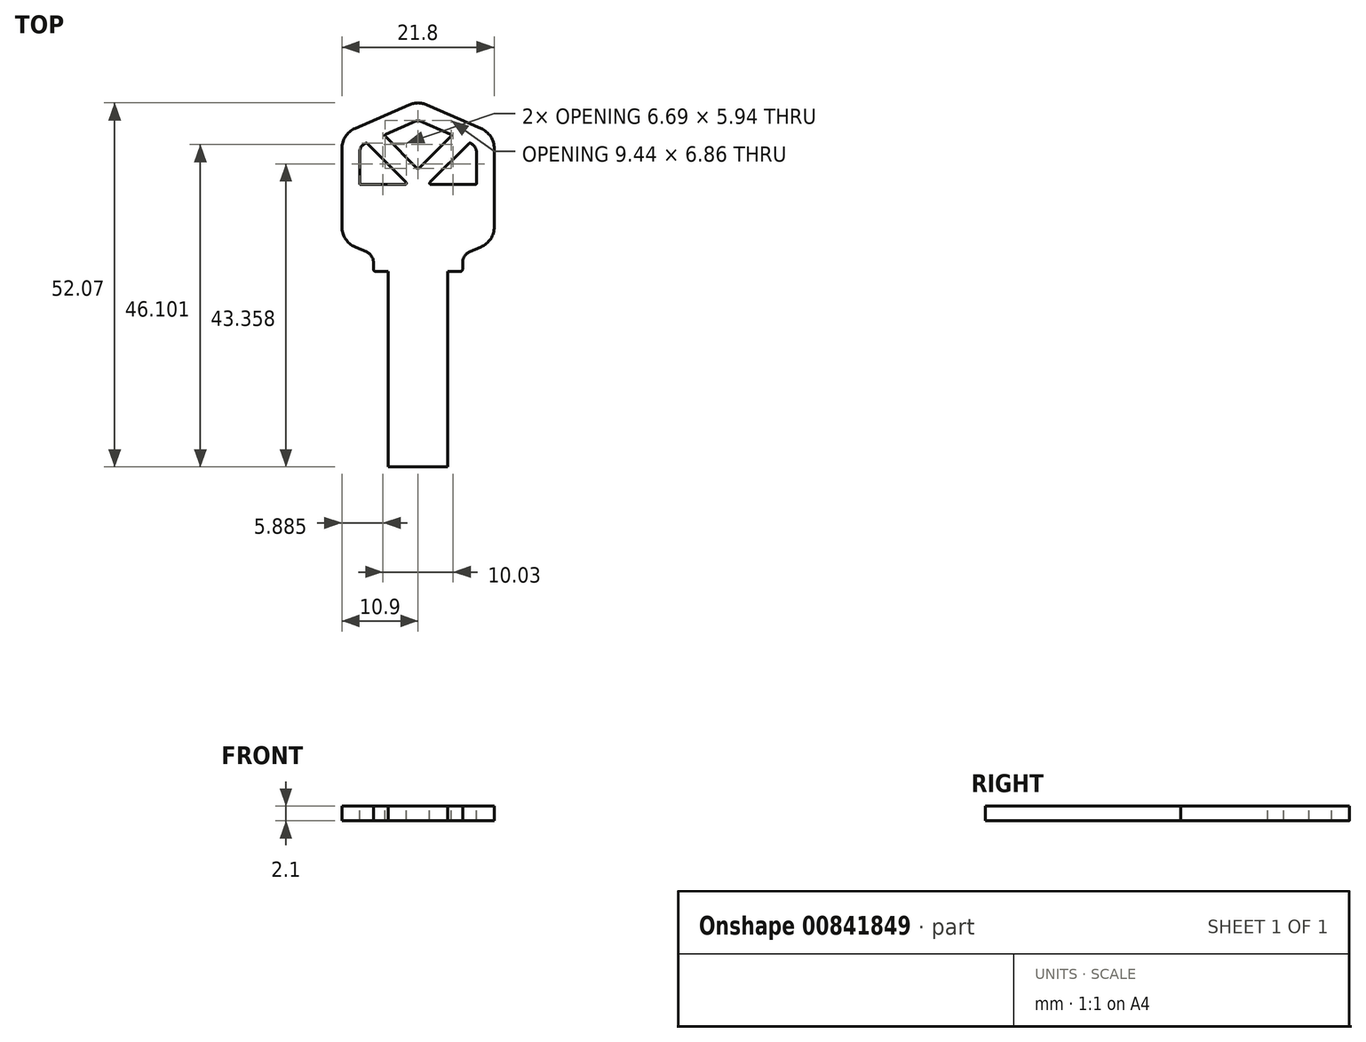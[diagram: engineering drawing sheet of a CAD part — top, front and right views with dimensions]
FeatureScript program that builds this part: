
annotation { "Feature Type Name" : "Feature", "Feature Type Description" : "" }
export const myFeature = defineFeature(function(context is Context, id is Id, definition is map)
    precondition{}
    {
        {
            var Q0;
            Q0=qCreatedBy(makeId("Top.planeOp"),FACE);
            var sketch = newSketch(context, id + "F0", { "sketchPlane" : qUnion([Q0])});
            skLineSegment(sketch, "E0", {"start": v(-1.27, -0.56) * mm, "end": v(-9, -3.93) * mm});
            skLineSegment(sketch, "E1", {"start": v(1.27, -0.56) * mm, "end": v(9, -3.93) * mm});
            skLineSegment(sketch, "E2", {"start": v(0, 0) * mm, "end": v(0, -52.36) * mm, "construction": true});
            skLineSegment(sketch, "E3", {"start": v(-10.9, -6.84) * mm, "end": v(-10.9, -17.99) * mm});
            skLineSegment(sketch, "E4", {"start": v(-9, -20.9) * mm, "end": v(-7.34, -21.62) * mm});
            skLineSegment(sketch, "E5", {"start": v(-6.39, -23.08) * mm, "end": v(-6.39, -24.42) * mm});
            skLineSegment(sketch, "E6", {"start": v(-6.39, -24.42) * mm, "end": v(-4.27, -24.42) * mm});
            skLineSegment(sketch, "E7", {"start": v(-4.27, -24.42) * mm, "end": v(-4.27, -52.36) * mm});
            skLineSegment(sketch, "E8", {"start": v(10.9, -6.84) * mm, "end": v(10.9, -17.99) * mm});
            skLineSegment(sketch, "E9", {"start": v(-10.9, -12.41) * mm, "end": v(0, -12.41) * mm, "construction": true});
            skLineSegment(sketch, "E10", {"start": v(0, -12.41) * mm, "end": v(10.9, -12.41) * mm, "construction": true});
            skLineSegment(sketch, "E11", {"start": v(9, -20.9) * mm, "end": v(7.34, -21.62) * mm});
            skLineSegment(sketch, "E12", {"start": v(6.39, -23.08) * mm, "end": v(6.39, -24.42) * mm});
            skLineSegment(sketch, "E13", {"start": v(6.39, -24.42) * mm, "end": v(4.27, -24.42) * mm});
            skLineSegment(sketch, "E14", {"start": v(4.27, -24.42) * mm, "end": v(4.27, -52.36) * mm});
            skLineSegment(sketch, "E15", {"start": v(-4.27, -52.36) * mm, "end": v(4.27, -52.36) * mm});
            skPoint(sketch, "E16.visualSharp", {"position": v(0, 0) * mm});
            skArc(sketch, "E16.filletArc", {"start": v(1.27, -0.56) * mm, "mid": v(0, -0.29) * mm, "end": v(-1.27, -0.56) * mm});
            skPoint(sketch, "E17.visualSharp", {"position": v(-10.9, -4.76) * mm});
            skArc(sketch, "E17.filletArc", {"start": v(-9, -3.93) * mm, "mid": v(-10.38, -5.1) * mm, "end": v(-10.9, -6.84) * mm});
            skPoint(sketch, "E18.visualSharp", {"position": v(10.9, -4.76) * mm});
            skArc(sketch, "E18.filletArc", {"start": v(10.9, -6.84) * mm, "mid": v(10.38, -5.1) * mm, "end": v(9, -3.93) * mm});
            skPoint(sketch, "E19", {"position": v(0, -0.29) * mm});
            skPoint(sketch, "E20.visualSharp", {"position": v(10.9, -20.07) * mm});
            skArc(sketch, "E20.filletArc", {"start": v(9, -20.9) * mm, "mid": v(10.38, -19.73) * mm, "end": v(10.9, -17.99) * mm});
            skPoint(sketch, "E21.visualSharp", {"position": v(-10.9, -20.07) * mm});
            skArc(sketch, "E21.filletArc", {"start": v(-10.9, -17.99) * mm, "mid": v(-10.38, -19.73) * mm, "end": v(-9, -20.9) * mm});
            skPoint(sketch, "E22.visualSharp", {"position": v(-6.39, -22.04) * mm});
            skArc(sketch, "E22.filletArc", {"start": v(-6.39, -23.08) * mm, "mid": v(-6.65, -22.2) * mm, "end": v(-7.34, -21.62) * mm});
            skPoint(sketch, "E23.visualSharp", {"position": v(6.39, -22.04) * mm});
            skArc(sketch, "E23.filletArc", {"start": v(7.34, -21.62) * mm, "mid": v(6.65, -22.2) * mm, "end": v(6.39, -23.08) * mm});
            skSolve(sketch);
        }
        {
            var Q0;
            Q0=makeQuery(id+"F0.imprint","IMPRINT",FACE,{"disambiguationData":[TD([[makeQuery(id+"F0.imprint","IMPRINT",EDGE,{"derivedFrom":sQuery(id+"F0.wireOp",EDGE,"E0")}),1.0]])]});
            extrude(context, id + "F1", {"entities" : qUnion([Q0]), "depth" : 2.1 * mm, "offsetDistance" : 25.4 * mm, "symmetric" : true});
        }
        {
            var Q0;
            Q0=makeQuery(id+"F1.opExtrude","SWEPT_EDGE",EDGE,{"disambiguationData":[OSD([sQuery(id+"F0.wireOp",EDGE,"E12"),sQuery(id+"F0.wireOp",EDGE,"E13")])]});
            var Q1;
            Q1=makeQuery(id+"F1.opExtrude","SWEPT_EDGE",EDGE,{"disambiguationData":[OSD([sQuery(id+"F0.wireOp",EDGE,"E5"),sQuery(id+"F0.wireOp",EDGE,"E6")])]});
            fillet(context, id + "F2", {"entities" : qUnion([Q0, Q1]), "radius" : 0.4 * mm, "tangentPropagation" : true, "allowEdgeOverflow" : false});
        }
        {
            var Q0;
            Q0=makeQuery(id+"F1.opExtrude","CAP_FACE",FACE,{"disambiguationData":[OSD([sQuery(id+"F0.wireOp",EDGE,"E0"),sQuery(id+"F0.wireOp",EDGE,"E1"),sQuery(id+"F0.wireOp",EDGE,"E3"),sQuery(id+"F0.wireOp",EDGE,"E4"),sQuery(id+"F0.wireOp",EDGE,"E5"),sQuery(id+"F0.wireOp",EDGE,"E6"),sQuery(id+"F0.wireOp",EDGE,"E7"),sQuery(id+"F0.wireOp",EDGE,"E8"),sQuery(id+"F0.wireOp",EDGE,"E11"),sQuery(id+"F0.wireOp",EDGE,"E12"),sQuery(id+"F0.wireOp",EDGE,"E13"),sQuery(id+"F0.wireOp",EDGE,"E14"),sQuery(id+"F0.wireOp",EDGE,"E15"),sQuery(id+"F0.wireOp",EDGE,"E16.filletArc"),sQuery(id+"F0.wireOp",EDGE,"E17.filletArc"),sQuery(id+"F0.wireOp",EDGE,"E18.filletArc"),sQuery(id+"F0.wireOp",EDGE,"E20.filletArc"),sQuery(id+"F0.wireOp",EDGE,"E21.filletArc"),sQuery(id+"F0.wireOp",EDGE,"E22.filletArc"),sQuery(id+"F0.wireOp",EDGE,"E23.filletArc")])],"isStart":false});
            var sketch = newSketch(context, id + "F3", { "sketchPlane" : qUnion([Q0])});
            skLineSegment(sketch, "E24.0", {"start": v(-8.36, -6.42) * mm, "end": v(-8.36, -11.78) * mm});
            skLineSegment(sketch, "E24.1", {"start": v(-0.25, -2.88) * mm, "end": v(-4.6, -4.78) * mm});
            skLineSegment(sketch, "E24.2", {"start": v(0.25, -2.88) * mm, "end": v(4.6, -4.78) * mm});
            skLineSegment(sketch, "E24.3", {"start": v(8.36, -6.42) * mm, "end": v(8.36, -11.78) * mm});
            skLineSegment(sketch, "E25", {"start": v(-8.16, -11.97) * mm, "end": v(-1.87, -11.97) * mm});
            skLineSegment(sketch, "E26", {"start": v(0, -11.97) * mm, "end": v(0, -2.77) * mm, "construction": true});
            skPoint(sketch, "E27.visualSharp", {"position": v(0, -2.77) * mm});
            skArc(sketch, "E27.filletArc", {"start": v(0.25, -2.88) * mm, "mid": v(0, -2.83) * mm, "end": v(-0.25, -2.88) * mm});
            skLineSegment(sketch, "E28", {"start": v(0.14, -9.63) * mm, "end": v(4.66, -5.1) * mm});
            skLineSegment(sketch, "E29", {"start": v(-0.14, -9.63) * mm, "end": v(-4.66, -5.1) * mm});
            skLineSegment(sketch, "E30", {"start": v(4.87, -4.9) * mm, "end": v(7.37, -6) * mm, "construction": true});
            skLineSegment(sketch, "E31", {"start": v(-4.87, -4.9) * mm, "end": v(-7.37, -6) * mm, "construction": true});
            skPoint(sketch, "E32.visualSharp", {"position": v(0, -9.77) * mm});
            skArc(sketch, "E32.filletArc", {"start": v(-0.14, -9.63) * mm, "mid": v(0, -9.69) * mm, "end": v(0.14, -9.63) * mm});
            skPoint(sketch, "E33", {"position": v(0, -9.69) * mm});
            skPoint(sketch, "E34", {"position": v(0, -2.83) * mm});
            skPoint(sketch, "E35.visualSharp", {"position": v(-4.87, -4.9) * mm});
            skArc(sketch, "E35.filletArc", {"start": v(-4.6, -4.78) * mm, "mid": v(-4.72, -4.93) * mm, "end": v(-4.66, -5.1) * mm});
            skPoint(sketch, "E36.visualSharp", {"position": v(4.87, -4.9) * mm});
            skArc(sketch, "E36.filletArc", {"start": v(4.66, -5.1) * mm, "mid": v(4.72, -4.93) * mm, "end": v(4.6, -4.78) * mm});
            skLineSegment(sketch, "E37", {"start": v(-7.27, -6.09) * mm, "end": v(-1.73, -11.64) * mm});
            skLineSegment(sketch, "E38", {"start": v(7.27, -6.09) * mm, "end": v(1.73, -11.64) * mm});
            skLineSegment(sketch, "E39", {"start": v(-1.39, -11.97) * mm, "end": v(1.39, -11.97) * mm, "construction": true});
            skLineSegment(sketch, "E40", {"start": v(1.87, -11.97) * mm, "end": v(8.16, -11.97) * mm});
            skLineSegment(sketch, "E41", {"start": v(-7.5, -6.05) * mm, "end": v(-8.36, -6.42) * mm});
            skLineSegment(sketch, "E42", {"start": v(7.5, -6.05) * mm, "end": v(8.36, -6.42) * mm});
            skPoint(sketch, "E43.visualSharp", {"position": v(-8.36, -11.97) * mm});
            skArc(sketch, "E43.filletArc", {"start": v(-8.36, -11.78) * mm, "mid": v(-8.3, -11.92) * mm, "end": v(-8.16, -11.97) * mm});
            skPoint(sketch, "E44.visualSharp", {"position": v(-1.39, -11.97) * mm});
            skArc(sketch, "E44.filletArc", {"start": v(-1.87, -11.97) * mm, "mid": v(-1.68, -11.85) * mm, "end": v(-1.73, -11.64) * mm});
            skPoint(sketch, "E45.visualSharp", {"position": v(1.39, -11.97) * mm});
            skArc(sketch, "E45.filletArc", {"start": v(1.73, -11.64) * mm, "mid": v(1.68, -11.85) * mm, "end": v(1.87, -11.97) * mm});
            skPoint(sketch, "E46.visualSharp", {"position": v(8.36, -11.97) * mm});
            skArc(sketch, "E46.filletArc", {"start": v(8.16, -11.97) * mm, "mid": v(8.3, -11.92) * mm, "end": v(8.36, -11.78) * mm});
            skPoint(sketch, "E47.visualSharp", {"position": v(-7.37, -6) * mm});
            skArc(sketch, "E47.filletArc", {"start": v(-7.27, -6.09) * mm, "mid": v(-7.38, -6.03) * mm, "end": v(-7.5, -6.05) * mm});
            skPoint(sketch, "E48.visualSharp", {"position": v(7.37, -6) * mm});
            skArc(sketch, "E48.filletArc", {"start": v(7.5, -6.05) * mm, "mid": v(7.38, -6.03) * mm, "end": v(7.27, -6.09) * mm});
            skArc(sketch, "E49", {"start": v(-7.5, -6.05) * mm, "mid": v(-8.12, -6.58) * mm, "end": v(-8.36, -7.37) * mm});
            skArc(sketch, "E50", {"start": v(8.36, -7.37) * mm, "mid": v(8.12, -6.58) * mm, "end": v(7.5, -6.05) * mm});
            skSolve(sketch);
        }
        {
            var Q0;
            Q0=makeQuery(id+"F3.imprint","IMPRINT",FACE,{"disambiguationData":[TD([[makeQuery(id+"F3.imprint","IMPRINT",EDGE,{"derivedFrom":sQuery(id+"F3.wireOp",EDGE,"E24.1")}),1.0]])]});
            var Q1;
            Q1=makeQuery(id+"F3.imprint","IMPRINT",FACE,{"disambiguationData":[TD([[makeQuery(id+"F3.imprint","IMPRINT",EDGE,{"derivedFrom":sQuery(id+"F3.wireOp",EDGE,"E25")}),1.0]])]});
            var Q2;
            Q2=makeQuery(id+"F3.imprint","IMPRINT",FACE,{"disambiguationData":[TD([[makeQuery(id+"F3.imprint","IMPRINT",EDGE,{"derivedFrom":sQuery(id+"F3.wireOp",EDGE,"E38")}),1.0]])]});
            extrude(context, id + "F4", {"entities" : qUnion([Q0, Q1, Q2]), "operationType" : NewBodyOperationType.REMOVE, "endBound" : BoundingType.THROUGH_ALL, "oppositeDirection" : true, "depth" : 25.4 * mm, "offsetDistance" : 25.4 * mm});
        }
    });
